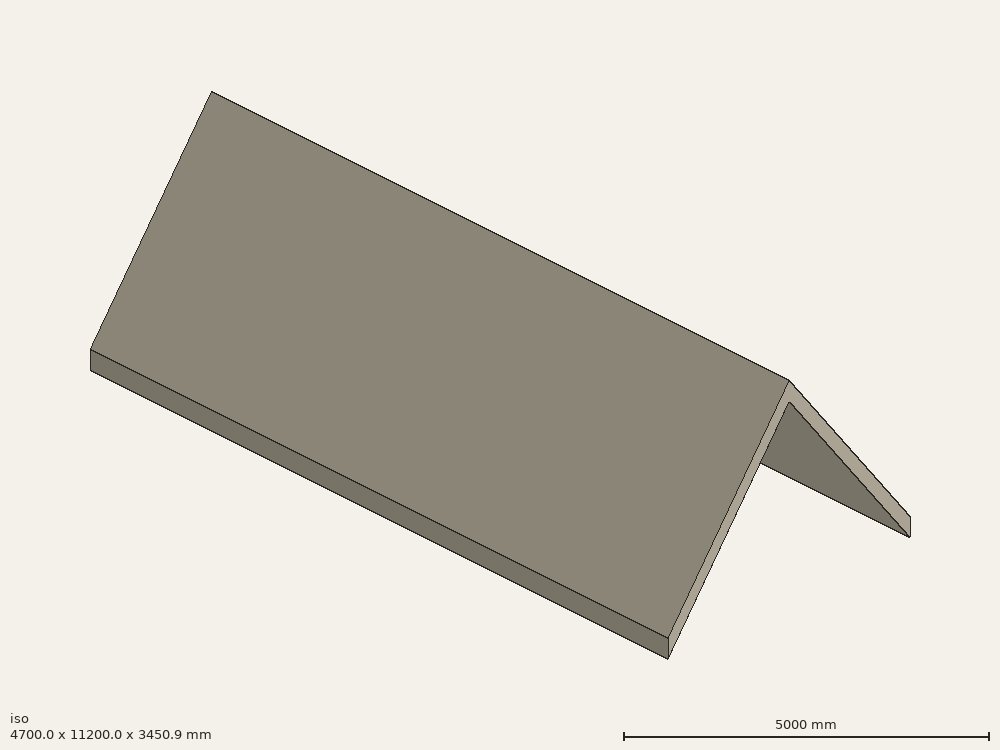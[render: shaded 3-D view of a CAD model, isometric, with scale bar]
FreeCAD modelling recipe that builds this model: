
FCSTD DOCUMENT  (FreeCAD 0.16R6706 (Git))
Label: Roof
License: All rights reserved
LicenseURL: http://en.wikipedia.org/wiki/All_rights_reserved
objects: Part::FeaturePython×3, Part::Part2DObjectPython×2, App::DocumentObjectGroupPython×1
note: 5 computed .brp shape members not serialized (recipe doc carries the construction recipe); baked Part::Feature solids carry a one-line shape summary decoded from their .brp

FEATURE [Part::Part2DObjectPython] DWire  # Draft 2D object (typed FeaturePython)
  ChamferSize = 0
  Closed = true
  End = (0,0,0)
  FilletRadius = 0
  Length = 31000
  MakeFace = false
  Points = (5) [(0,0,0),(0,-11000,0),(4500,-11000,0),(4500,0,0),(0,0,0)]
  Start = (0,0,0)
  Subdivisions = 0
FEATURE [Part::FeaturePython] Roof003  # WARN: FeaturePython — macro-defined, semantics opaque (R4)
  Face = 0
  MoveWithHost = false
  Role = 0
FEATURE [App::DocumentObjectGroupPython] Building  # scripted group (container) (typed FeaturePython)
  BuildingType = 0
  Group = -> [DWire,Roof003]
  Height = 0
FEATURE [Part::Part2DObjectPython] Rectangle  # Draft 2D object (typed FeaturePython)
  ChamferSize = 0
  Columns = 1
  FilletRadius = 0
  Height = -2471.85
  Length = -2113.3
  MakeFace = true
  Placement = pos=(2818.79,-8082.85,2563.37) rot=(0.446198,0,0.894934;3.14159rad)
  Rows = 1
FEATURE [Part::FeaturePython] Window  # WARN: FeaturePython — macro-defined, semantics opaque (R4)
  Base = -> Rectangle
  Height = 0
  HoleDepth = 0
  MoveWithHost = true
  Normal = (-0.798636,0,-0.601815)
  Preset = 0
  Role = 0
  Width = 0
  WindowParts = Default | Frame | Wire0 | 1 | 0
FEATURE [Part::FeaturePython] Roof  # WARN: FeaturePython — macro-defined, semantics opaque (R4)
  Base = -> Roof003
  Face = 0
  MoveWithHost = false
  Role = 0
  Subtractions = -> [Window]
